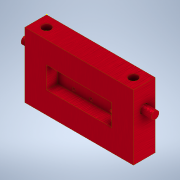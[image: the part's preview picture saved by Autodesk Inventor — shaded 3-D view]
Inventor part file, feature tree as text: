
AUTODESK INVENTOR PART (.ipt)
format: ipt  version: 2021.3 (Build 253353000, 353)  size: 238,080 bytes
history: native  units: mm
features: sketch x12, extrude x10
ambient origin geometry x8: Origin, YZ Plane, XZ Plane, XY Plane, X Axis, Y Axis, Z Axis, Center Point
bodies: Solid1 (feature_tree)
feature tree (22):
  extrude  "Extrusion1"  Depth=100.0mm
  extrude  "Extrusion2"  Depth=20.0mm
  extrude  "Extrusion3"  Depth=20.0mm
  sketch  "Sketch4"  dims[d7=20.0mm d8=60.0mm]
  sketch  "Sketch5"  dims[d9=20.0mm d10=10.0mm d11=0.0mm]
  extrude  "Extrusion4"  Depth=20.0mm
  extrude  "Extrusion5"  Depth=10.0mm TaperAngle=0.0deg
  extrude  "Extrusion6"  Depth=10.0mm TaperAngle=0.0deg
  extrude  "Extrusion7"  Depth=20.0mm
  extrude  "Extrusion8"  Depth=80.0mm
  sketch  "Sketch10"  dims[d33=8.0mm d34=80.0mm]
  extrude  "Extrusion9"  Depth=8.0mm
  extrude  "Extrusion10"  Depth=80.0mm
  sketch  "Sketch1"  dims[d0=100.0mm d1=60.0mm]
  sketch  "Sketch2"  dims[d2=20.0mm d3=0.0mm d4=20.0mm]
  sketch  "Sketch3"  dims[d5=20.0mm d6=20.0mm]
  sketch  "Sketch6"  dims[d12=8.0mm d14=10.0mm d15=0.0mm]
  sketch  "Sketch7"  dims[d21=20.0mm d27=8.0mm]
  sketch  "Sketch8"  dims[d28=8.0mm d29=80.0mm]
  sketch  "Sketch9"  dims[d30=5.0mm d31=0.0mm d32=8.0mm]
  sketch  "Sketch11"  dims[d35=10.0mm]
  sketch  "Sketch12"  dims[d36=10.0mm d37=5.0mm d38=0.0mm d39=3.0mm d40=3.0mm d41=3.0mm d42=5.0mm d43=0.0mm d44=5.0mm d45=0.0mm d46=3.0mm d47=3.0mm d48=3.0mm d49=5.0mm d50=0.0mm d51=7.0mm d52=20.0mm d53=0.0mm d54=20.0mm d55=0.0mm]
